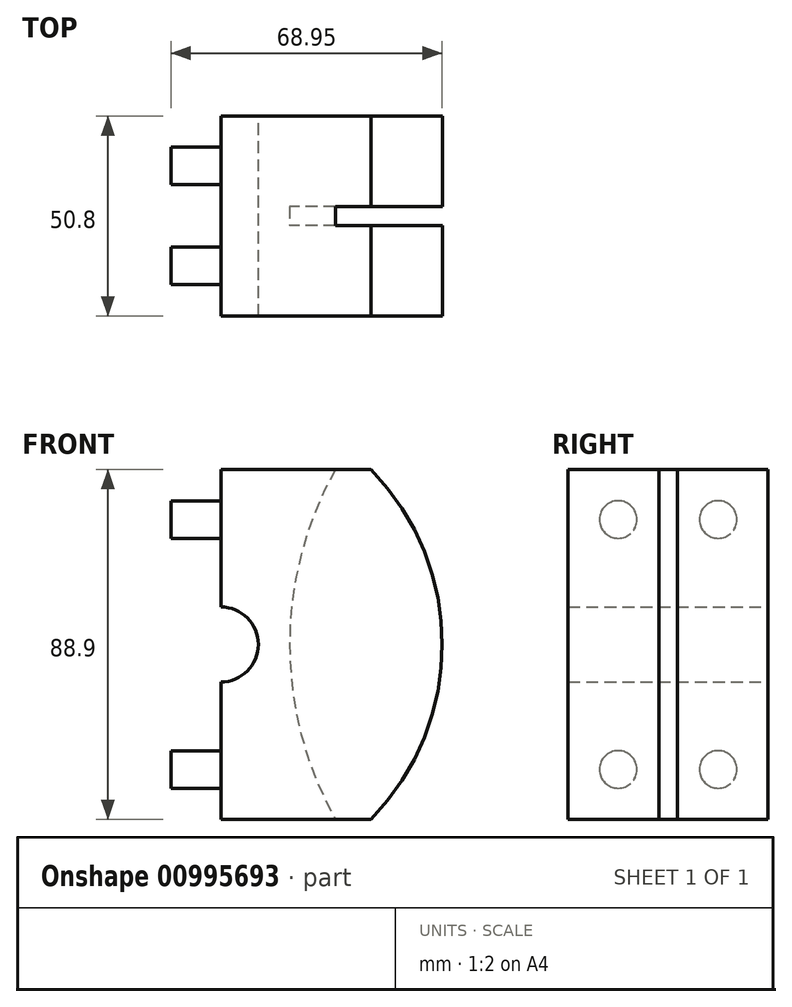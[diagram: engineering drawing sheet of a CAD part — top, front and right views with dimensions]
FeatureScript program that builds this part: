
annotation { "Feature Type Name" : "Feature", "Feature Type Description" : "" }
export const myFeature = defineFeature(function(context is Context, id is Id, definition is map)
    precondition{}
    {
        {
            var Q0;
            Q0=qCreatedBy(makeId("Front.planeOp"),FACE);
            var sketch = newSketch(context, id + "F0", { "sketchPlane" : qUnion([Q0])});
            skLineSegment(sketch, "E0", {"start": v(0, -44.45) * mm, "end": v(0, -9.53) * mm});
            skLineSegment(sketch, "E1", {"start": v(0, 44.45) * mm, "end": v(38.1, 44.45) * mm});
            skLineSegment(sketch, "E2", {"start": v(0, -44.45) * mm, "end": v(38.1, -44.45) * mm});
            skArc(sketch, "E3", {"start": v(38.1, -44.45) * mm, "mid": v(56.25, 0) * mm, "end": v(38.1, 44.45) * mm});
            skArc(sketch, "E4", {"start": v(0, -9.53) * mm, "mid": v(9.53, 0) * mm, "end": v(0, 9.53) * mm});
            skLineSegment(sketch, "E5.trimOffspring", {"start": v(0, 9.53) * mm, "end": v(0, 44.45) * mm});
            skCircle(sketch, "E6", {"center": v(101.6, 0) * mm, "radius": 88.9 * mm, "construction": true});
            skSolve(sketch);
        }
        {
            var Q0;
            Q0=makeQuery(id+"F0.imprint","IMPRINT",FACE,{"disambiguationData":[TD([[makeQuery(id+"F0.imprint","IMPRINT",EDGE,{"derivedFrom":sQuery(id+"F0.wireOp",EDGE,"E0")}),-1.0]])]});
            extrude(context, id + "F1", {"entities" : qUnion([Q0]), "endBound" : BoundingType.SYMMETRIC, "depth" : 50.8 * mm, "offsetDistance" : 25.4 * mm});
        }
        {
            var Q0;
            Q0=qCreatedBy(makeId("Front.planeOp"),FACE);
            var sketch = newSketch(context, id + "F2", { "sketchPlane" : qUnion([Q0])});
            skCircle(sketch, "E7", {"center": v(107.95, 0) * mm, "radius": 90.49 * mm});
            skSolve(sketch);
        }
        {
            var Q0;
            Q0=makeQuery(id+"F2.imprint","IMPRINT",FACE,{"disambiguationData":[TD([[makeQuery(id+"F2.imprint","IMPRINT",EDGE,{"derivedFrom":sQuery(id+"F2.wireOp",EDGE,"E7")}),1.0]])]});
            extrude(context, id + "F3", {"entities" : qUnion([Q0]), "operationType" : NewBodyOperationType.REMOVE, "endBound" : BoundingType.SYMMETRIC, "oppositeDirection" : true, "depth" : 4.76 * mm, "offsetDistance" : 25.4 * mm});
        }
        {
            var Q0;
            Q0=qCreatedBy(makeId("Right.planeOp"),FACE);
            var sketch = newSketch(context, id + "F4", { "sketchPlane" : qUnion([Q0])});
            skCircle(sketch, "E8", {"center": v(12.7, 31.75) * mm, "radius": 4.76 * mm});
            skCircle(sketch, "E9", {"center": v(-12.7, 31.75) * mm, "radius": 4.76 * mm});
            skCircle(sketch, "E10", {"center": v(-12.7, -31.75) * mm, "radius": 4.76 * mm});
            skCircle(sketch, "E11", {"center": v(12.7, -31.75) * mm, "radius": 4.76 * mm});
            skLineSegment(sketch, "E12", {"start": v(12.7, -31.75) * mm, "end": v(12.7, -44.45) * mm, "construction": true});
            skLineSegment(sketch, "E13", {"start": v(12.7, -31.75) * mm, "end": v(25.4, -31.75) * mm, "construction": true});
            skLineSegment(sketch, "E14", {"start": v(-12.7, 44.45) * mm, "end": v(-12.7, 31.75) * mm, "construction": true});
            skLineSegment(sketch, "E15", {"start": v(-25.4, 31.75) * mm, "end": v(-12.7, 31.75) * mm, "construction": true});
            skSolve(sketch);
        }
        {
            var Q0;
            Q0=qSketchRegion(id+"F4",true);
            extrude(context, id + "F5", {"entities" : qUnion([Q0]), "operationType" : NewBodyOperationType.ADD, "oppositeDirection" : true, "depth" : 12.7 * mm, "offsetDistance" : 25.4 * mm});
        }
    });
